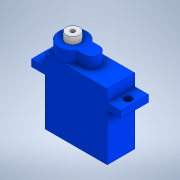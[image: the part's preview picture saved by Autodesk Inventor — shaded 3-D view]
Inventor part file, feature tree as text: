
AUTODESK INVENTOR PART (.ipt)
format: ipt  version: 2020 (Build 240168000, 168)  size: 170,496 bytes
history: native  units: mm
features: extrude x4, sketch x4
ambient origin geometry x8: Origin, YZ Plane, XZ Plane, XY Plane, X Axis, Y Axis, Z Axis, Center Point
bodies: Solid1 (feature_tree)
feature tree (8):
  extrude  "Extrusion1"  Depth=22.45mm
  extrude  "Extrusion2"  Depth=17.0mm
  extrude  "Extrusion3"  Depth=4.9mm
  extrude  "Extrusion4"  Depth=2.55mm
  sketch  "Sketch1"  dims[d0=23.75mm d1=22.45mm]
  sketch  "Sketch2"  dims[d2=2.45mm d3=17.0mm]
  sketch  "Sketch3"  dims[d4=4.9mm d5=4.9mm]
  sketch  "Sketch4"  dims[d6=10.0mm d7=0.0mm d8=2.77mm d9=27.5mm d10=10.0mm d11=0.0mm d12=5.5mm d13=14.6mm d14=4.3mm d15=0.0mm d16=4.84mm d17=1.5mm d18=2.55mm d19=0.0mm]
